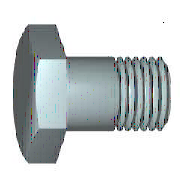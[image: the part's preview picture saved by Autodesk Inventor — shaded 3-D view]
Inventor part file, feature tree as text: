
AUTODESK INVENTOR PART (.ipt)
format: ipt  version: 2025 (Build 290162010, 162A)  size: 193,536 bytes
history: native  units: mm (DEFAULTED — no unit token found)
features: extrude x1, chamfer x1, plane x1
ambient origin geometry x7: Origin, YZ Plane, XZ Plane, X Axis, Y Axis, Z Axis, Center Point
bodies: Solid1 (feature_tree), Body (feature_tree)
feature tree (3):
  extrude  "Head"  Depth=30.0mm
  chamfer  "Chamfer1"  Distance=25.5mm
  plane  "Work Plane1"
